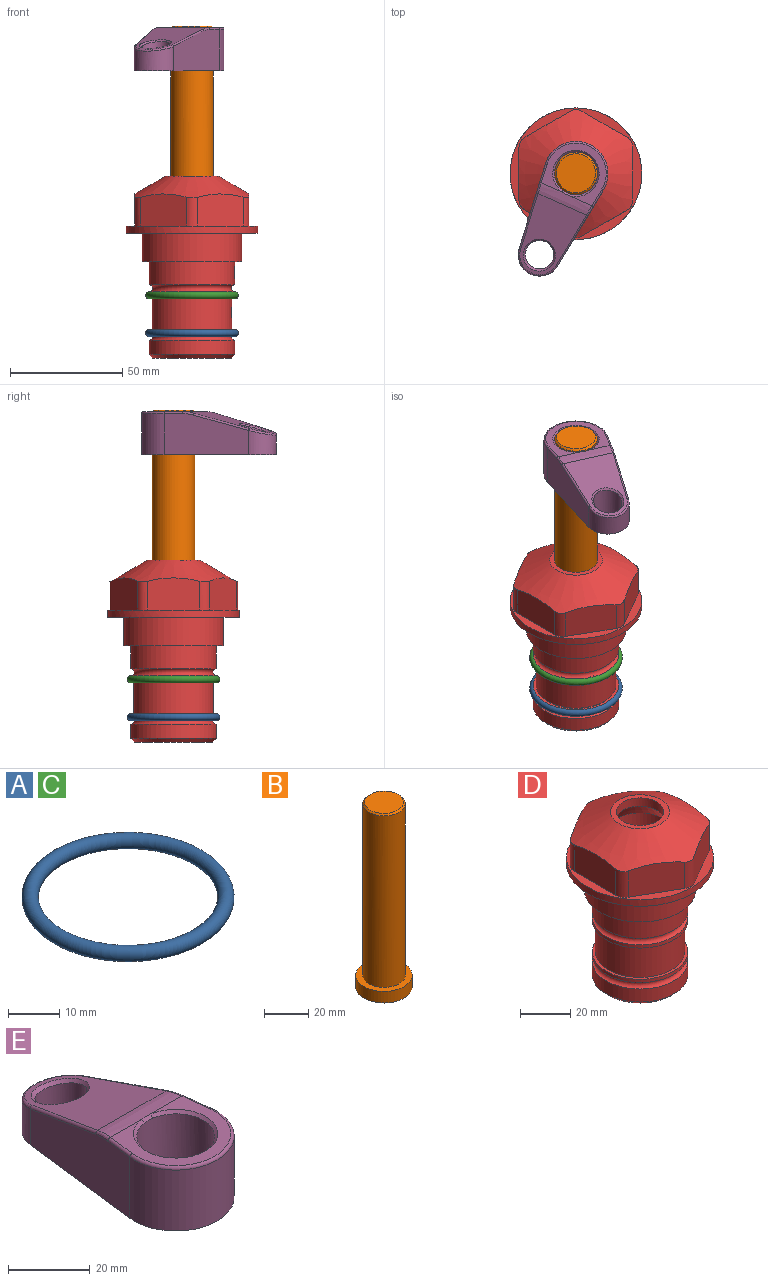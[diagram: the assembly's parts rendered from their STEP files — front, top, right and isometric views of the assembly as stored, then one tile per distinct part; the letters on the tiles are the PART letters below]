
ASSEMBLY  parts=5 mates=4
PART A: 1 faces, bbox 44.7x44.7x3.2 mm
  f0: torus R=19.05mm, axis (0,0,1), area 1193.9mm2
PART B: 6 faces, bbox 25.4x25.4x101.6 mm
  f0: plane 17.46x17.46mm, normal (0,0,1), area 239.5mm2, adj f5
  f1: plane 25.4x25.4mm, normal (0,0,-1), area 506.7mm2, adj f2
  f2: cylinder r=12.7mm len=25.4mm, axis (0,0,1), area 506.7mm2, adj f1,f3
  f3: plane 25.4x25.4mm, normal (0,0,1), area 221.7mm2, adj f2,f4
  f4: cylinder r=9.53mm len=94.46mm, axis (0,0,1), area 5653mm2, adj f3,f5
  f5: cone r=8.73mm half-angle=45deg, axis (0,0,-1), area 64.4mm2, adj f0,f4
PART C: same geometry as A
PART D: 36 faces, bbox 58.7x58.7x81 mm
  f0: cylinder r=17.78mm len=35.56mm, axis (0,0,1), area 1670.8mm2, adj f23,f24,f31
  f1: cylinder r=19.05mm len=38.1mm, axis (0,0,1), area 1191.9mm2, adj f26,f27,f30
  f2: plane 58.66x58.66mm, normal (0,0,-1), area 1150.6mm2, adj f3,f28
  f3: cylinder r=29.33mm len=58.66mm, axis (0,0,-1), area 585.1mm2, adj f2,f4
  f4: plane 58.66x58.66mm, normal (0,0,1), area 475.9mm2, adj f3,f5,f6,f7,f8,f9,f10,f11
  f5: plane 20.32x14.34mm, normal (-0.5,0.87,0), area 324.4mm2, adj f4,f15,f16,f17
  f6: plane 20.32x14.34mm, normal (0.5,0.87,0), area 324.4mm2, adj f4,f14,f15,f17
  f7: plane 23.48x14.34mm, normal (1,0,0), area 324.4mm2, adj f4,f13,f14,f17
  f8: plane 20.32x14.34mm, normal (0.5,-0.87,0), area 324.4mm2, adj f4,f12,f13,f17
  f9: plane 20.32x14.34mm, normal (-0.5,-0.87,0), area 324.4mm2, adj f4,f11,f12,f17
  f10: plane 23.48x14.34mm, normal (-1,0,0), area 324.4mm2, adj f4,f11,f16,f17
  f11: cylinder r=5.08mm len=12.85mm, axis (0,0,-1), area 67.2mm2, adj f4,f9,f10,f17
  f12: cylinder r=5.08mm len=12.85mm, axis (0,0,-1), area 67.2mm2, adj f4,f8,f9,f17
  f13: cylinder r=5.08mm len=12.85mm, axis (0,0,-1), area 67.2mm2, adj f4,f7,f8,f17
  f14: cylinder r=5.08mm len=12.85mm, axis (0,0,-1), area 67.2mm2, adj f4,f6,f7,f17
  f15: cylinder r=5.08mm len=12.85mm, axis (0,0,-1), area 67.2mm2, adj f4,f5,f6,f17
  f16: cylinder r=5.08mm len=12.85mm, axis (0,0,-1), area 67.2mm2, adj f4,f5,f10,f17
  f17: cone r=11.73mm half-angle=60deg, axis (0,0,-1), area 2071.8mm2, adj f5,f6,f7,f8,f9,f10,f11,f12
  f18: plane 23.46x23.46mm, normal (0,0,1), area 147.4mm2, adj f17,f35
  f19: plane 34.93x34.93mm, normal (0,0,-1), area 958mm2, adj f29
  f20: cylinder r=19.05mm len=38.1mm, axis (0,0,1), area 760.1mm2, adj f21,f29
  f21: torus R=19.05mm, axis (0,0,1), area 565.3mm2, adj f20,f22
  f22: cylinder r=19.05mm len=38.1mm, axis (0,0,1), area 190mm2, adj f21,f23
  f23: plane 38.1x38.1mm, normal (0,0,1), area 146.9mm2, adj f0,f22
  f24: plane 38.1x38.1mm, normal (0,0,-1), area 146.9mm2, adj f0,f25
  f25: cylinder r=19.05mm len=38.1mm, axis (0,0,1), area 190mm2, adj f24,f26
  f26: torus R=19.05mm, axis (0,0,1), area 565.3mm2, adj f1,f25
  f27: plane 44.45x44.45mm, normal (0,0,-1), area 411.7mm2, adj f1,f28
  f28: cylinder r=22.23mm len=44.45mm, axis (0,0,1), area 1773.5mm2, adj f2,f27
  f29: cone r=19.05mm half-angle=45deg, axis (0,0,1), area 257.5mm2, adj f19,f20
  f30: cylinder r=3.17mm len=6.75mm, axis (-1,0,0), area 128mm2, adj f1,f33
  f31: cylinder r=3.17mm len=6.35mm, axis (-1,0,0), area 102.5mm2, adj f0,f33
  f32: plane 25.4x25.4mm, normal (0,0,1), area 506.7mm2, adj f33
  f33: cylinder r=12.7mm len=66.42mm, axis (0,0,-1), area 5236.2mm2, adj f30,f31,f32,f34
  f34: cone r=9.53mm half-angle=30deg, axis (0,0,-1), area 443.4mm2, adj f33,f35
  f35: cylinder r=9.53mm len=19.05mm, axis (0,0,-1), area 240.9mm2, adj f18,f34
PART E: 31 faces, bbox 31.7x65.5x19.8 mm
  f0: plane 39.12x18.26mm, normal (0.99,0.12,0), area 612.2mm2, adj f1,f4,f7,f11,f13,f15
  f1: cylinder r=9.53mm len=18.91mm, axis (0,0,-1), area 296.1mm2, adj f0,f2,f7,f17
  f2: plane 39.12x18.26mm, normal (-0.99,0.12,0), area 612.2mm2, adj f1,f4,f7,f12,f14,f16
  f3: cylinder r=6.35mm len=12.7mm, axis (0,0,-1), area 362.4mm2, adj f7,f18
  f4: cylinder r=14.29mm len=28.58mm, axis (0,0,-1), area 882.2mm2, adj f0,f2,f7,f10
  f5: cylinder r=9.53mm len=19.05mm, axis (0,0,-1), area 1092.6mm2, adj f7,f19,f20
  f6: plane 26.99x23.69mm, normal (0,0,1), area 216.2mm2, adj f9,f10,f11,f12,f19
  f7: plane 63.5x28.58mm, normal (0,0,-1), area 661.8mm2, adj f0,f1,f2,f3,f4,f5,f22,f23
  f8: plane 33.52x23.6mm, normal (0,0.26,0.97), area 486mm2, adj f9,f15,f16,f17,f18
  f9: cylinder r=19.05mm len=24.72mm, axis (1,0,0), area 120.4mm2, adj f6,f8,f13,f14,f20
  f10: torus R=13.49mm, axis (0,0,1), area 59mm2, adj f4,f6,f11,f12
  f11: cylinder r=0.79mm len=8.67mm, axis (0.12,-0.99,0), area 10.8mm2, adj f0,f6,f10,f13
  f12: cylinder r=0.79mm len=8.67mm, axis (0.12,0.99,0), area 10.8mm2, adj f2,f6,f10,f14
  f13: bspline ~4.95x1.42mm, area 6.1mm2, adj f0,f9,f11,f15
  f14: bspline ~4.95x1.42mm, area 6.1mm2, adj f2,f9,f12,f16
  f15: cylinder r=0.79mm len=25.95mm, axis (0.12,-0.96,0.26), area 32.9mm2, adj f0,f8,f13,f17
  f16: cylinder r=0.79mm len=25.95mm, axis (0.12,0.96,-0.26), area 32.9mm2, adj f2,f8,f14,f17
  f17: bspline ~18.91x8.38mm, area 30mm2, adj f1,f8,f15,f16
  f18: bspline ~14.29x14.29mm, area 48.3mm2, adj f3,f8
  f19: cone r=9.53mm half-angle=45deg, axis (0,0,1), area 66.5mm2, adj f5,f6,f20
  f20: bspline ~3.22x0.96mm, area 3.5mm2, adj f5,f9,f19
  f21: plane 2.75x2.72mm, normal (0,0,-1), area 2.9mm2, adj f23,f25,f28
  f22: plane 23.05x15.88mm, normal (-0.99,-0.12,0), area 323.6mm2, adj f7,f25,f26,f27,f28,f29
  f23: plane 23.05x15.88mm, normal (0.99,-0.12,0), area 323.6mm2, adj f7,f21,f25,f27,f28,f30
  f24: cylinder r=9.53mm len=10.69mm, axis (0,0,-1), area 114.7mm2, adj f7,f27,f29,f30
  f25: cylinder r=12.7mm len=20.59mm, axis (0,0,-1), area 381.1mm2, adj f7,f21,f22,f23,f26,f28
  f26: plane 2.75x2.72mm, normal (0,0,-1), area 2.9mm2, adj f22,f25,f28
  f27: plane 19.72x18.37mm, normal (0,-0.26,-0.97), area 291.8mm2, adj f22,f23,f24,f28,f29,f30
  f28: cylinder r=15.88mm len=19.92mm, axis (1,0,0), area 54.8mm2, adj f21,f22,f23,f25,f26,f27
  f29: cylinder r=1.59mm len=11mm, axis (0,0,-1), area 34.7mm2, adj f7,f22,f24,f27
  f30: cylinder r=1.59mm len=11mm, axis (0,0,-1), area 34.7mm2, adj f7,f23,f24,f27
PLACE A t=(-2.22,-5.3,-15.1)mm
PLACE B rot(axis=(0,0,1),155.9deg) t=(-2.22,-5.3,33.72)mm
PLACE C t=(-2.22,-5.3,1.72)mm
PLACE D t=(-2.22,-5.3,4.9)mm fixed
PLACE E rot(axis=(0,0,1),155.9deg) t=(-2.22,-5.3,32.93)mm
MATE cylindrical B.f2 <-> D.f0  axis (0,0,1) through (-2.22,-5.3,1.97)mm
MATE fastened A.f0 <-> D.f0  axis (0,0,1) through (-2.22,-5.3,-39.61)mm
MATE fastened B.f2 <-> E.f4  axis (0,0,1) through (-2.22,-5.3,96.43)mm
MATE fastened C.f0 <-> D.f0  axis (0,0,1) through (-2.22,-5.3,-22.79)mm
